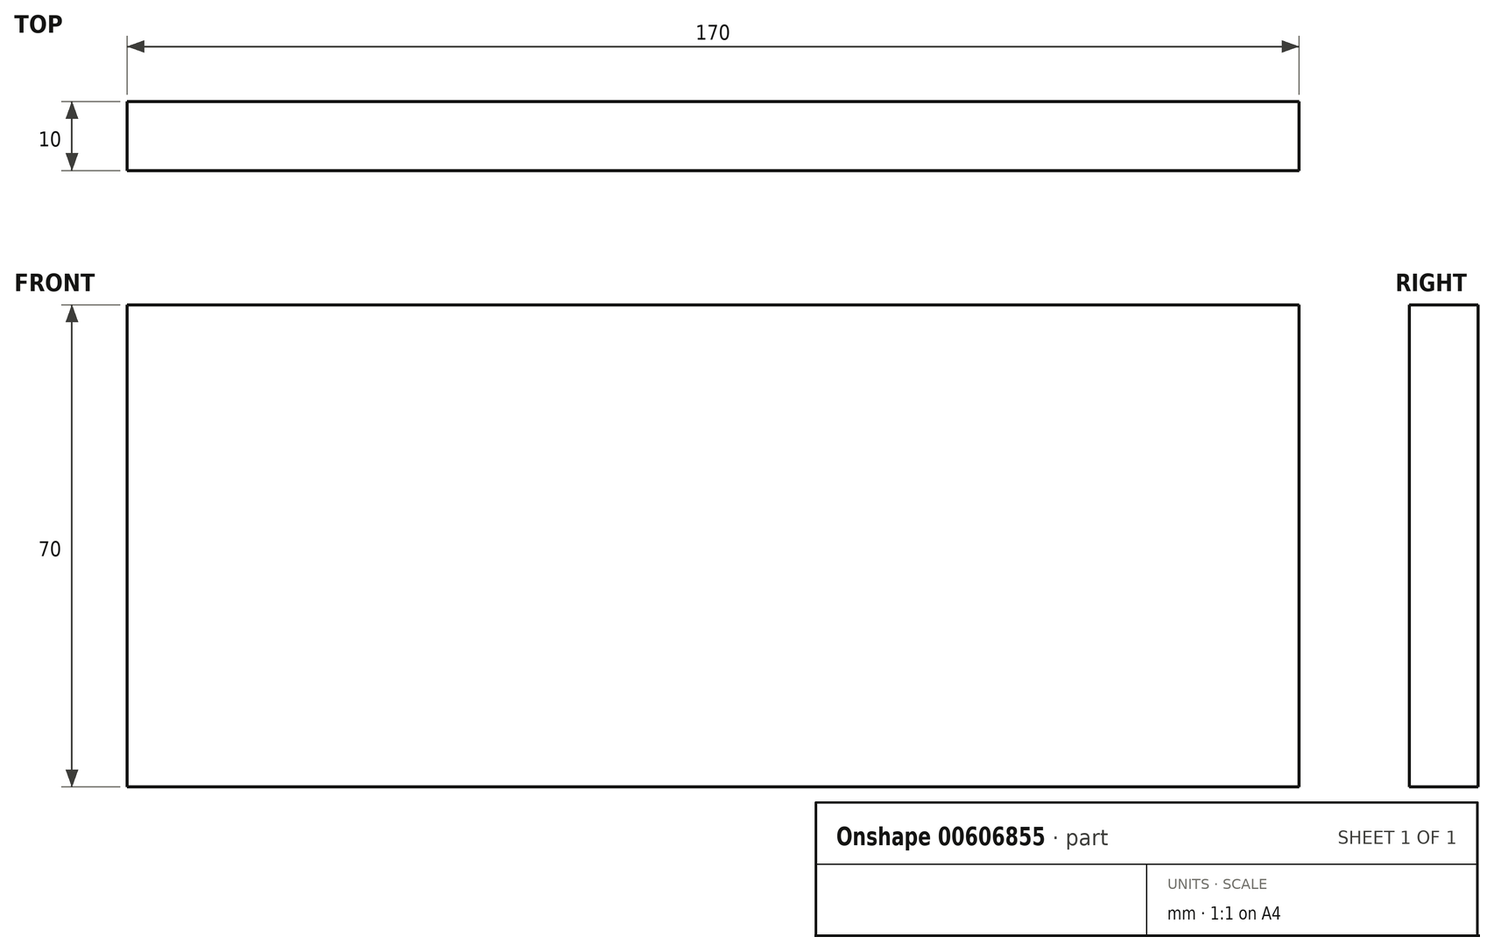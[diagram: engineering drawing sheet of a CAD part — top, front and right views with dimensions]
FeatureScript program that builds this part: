
annotation { "Feature Type Name" : "Feature", "Feature Type Description" : "" }
export const myFeature = defineFeature(function(context is Context, id is Id, definition is map)
    precondition{}
    {
        {
            var Q0;
            Q0=qCreatedBy(makeId("Front.planeOp"),FACE);
            var sketch = newSketch(context, id + "F0", { "sketchPlane" : qUnion([Q0])});
            skLineSegment(sketch, "E0.bottom", {"start": v(-71.39, 38.94) * mm, "end": v(98.61, 38.94) * mm});
            skLineSegment(sketch, "E0.top", {"start": v(-71.39, -31.06) * mm, "end": v(98.61, -31.06) * mm});
            skLineSegment(sketch, "E0.left", {"start": v(-71.39, 38.94) * mm, "end": v(-71.39, -31.06) * mm});
            skLineSegment(sketch, "E0.right", {"start": v(98.61, 38.94) * mm, "end": v(98.61, -31.06) * mm});
            skSolve(sketch);
        }
        {
            var Q0;
            Q0=qSketchRegion(id+"F0",true);
            extrude(context, id + "F1", {"entities" : qUnion([Q0]), "depth" : 10 * mm, "offsetDistance" : 25 * mm});
        }
    });
